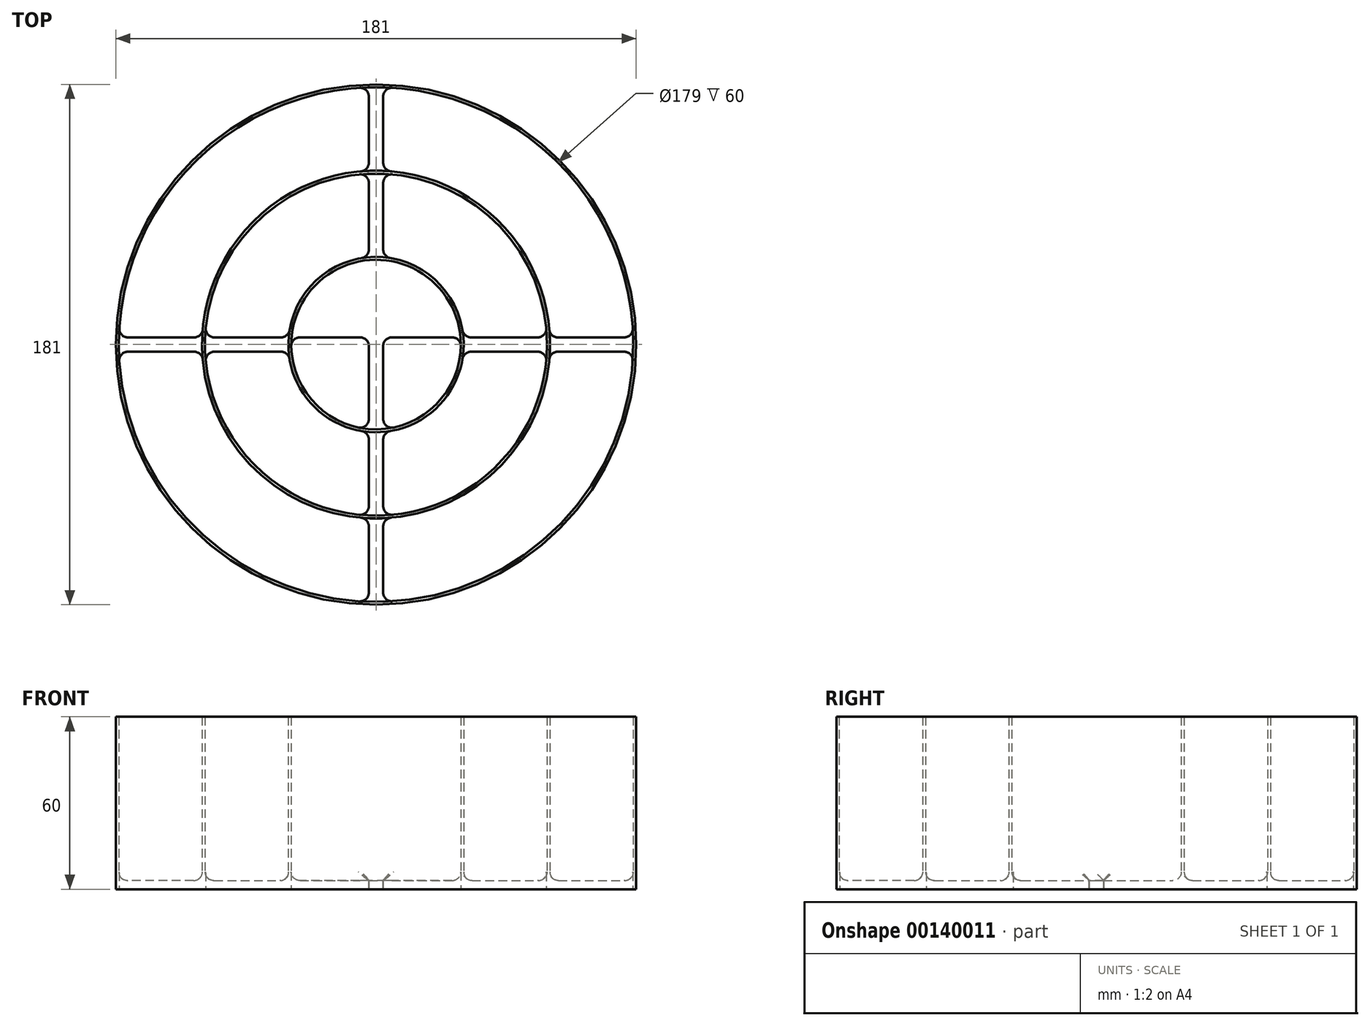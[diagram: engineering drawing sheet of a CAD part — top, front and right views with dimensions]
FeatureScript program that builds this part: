
annotation { "Feature Type Name" : "Feature", "Feature Type Description" : "" }
export const myFeature = defineFeature(function(context is Context, id is Id, definition is map)
    precondition{}
    {
        {
            var Q0;
            Q0=qCreatedBy(makeId("Top.planeOp"),FACE);
            var sketch = newSketch(context, id + "F2", { "sketchPlane" : qUnion([Q0])});
            skCircle(sketch, "E0", {"center": v(0, 0) * mm, "radius": 90.5 * mm});
            skCircle(sketch, "E1", {"center": v(0, 0) * mm, "radius": 89.5 * mm});
            skCircle(sketch, "E2", {"center": v(0, 0) * mm, "radius": 60.5 * mm});
            skCircle(sketch, "E3", {"center": v(0, 0) * mm, "radius": 59.5 * mm});
            skCircle(sketch, "E4", {"center": v(0, 0) * mm, "radius": 30.5 * mm});
            skCircle(sketch, "E5", {"center": v(0, 0) * mm, "radius": 29.5 * mm});
            skLineSegment(sketch, "E6", {"start": v(-59.45, 2.5) * mm, "end": v(-30.4, 2.5) * mm});
            skLineSegment(sketch, "E7", {"start": v(-59.45, -2.5) * mm, "end": v(-30.4, -2.5) * mm});
            skLineSegment(sketch, "E8", {"start": v(-60.45, 2.5) * mm, "end": v(-89.47, 2.5) * mm});
            skLineSegment(sketch, "E9", {"start": v(-60.45, -2.5) * mm, "end": v(-89.47, -2.5) * mm});
            skLineSegment(sketch, "E10", {"start": v(-29.4, 2.5) * mm, "end": v(29.4, 2.5) * mm});
            skLineSegment(sketch, "E11", {"start": v(-29.4, -2.5) * mm, "end": v(29.4, -2.5) * mm});
            skLineSegment(sketch, "E12", {"start": v(30.4, 2.5) * mm, "end": v(59.45, 2.5) * mm});
            skLineSegment(sketch, "E13", {"start": v(60.45, 2.5) * mm, "end": v(89.47, 2.5) * mm});
            skLineSegment(sketch, "E14", {"start": v(30.4, -2.5) * mm, "end": v(59.45, -2.5) * mm});
            skLineSegment(sketch, "E15", {"start": v(60.45, -2.5) * mm, "end": v(89.47, -2.5) * mm});
            skLineSegment(sketch, "E16", {"start": v(2.5, -60.45) * mm, "end": v(2.5, -89.47) * mm});
            skLineSegment(sketch, "E17", {"start": v(-2.5, -60.45) * mm, "end": v(-2.5, -89.47) * mm});
            skLineSegment(sketch, "E18", {"start": v(2.5, -59.45) * mm, "end": v(2.5, -30.4) * mm});
            skLineSegment(sketch, "E19", {"start": v(-2.5, -59.45) * mm, "end": v(-2.5, -30.4) * mm});
            skLineSegment(sketch, "E20", {"start": v(2.5, -29.4) * mm, "end": v(2.5, 29.4) * mm});
            skLineSegment(sketch, "E21", {"start": v(-2.5, -29.4) * mm, "end": v(-2.5, 29.4) * mm});
            skLineSegment(sketch, "E22", {"start": v(2.5, 30.4) * mm, "end": v(2.5, 59.45) * mm});
            skLineSegment(sketch, "E23", {"start": v(-2.5, 30.4) * mm, "end": v(-2.5, 59.45) * mm});
            skLineSegment(sketch, "E24", {"start": v(2.5, 60.45) * mm, "end": v(2.5, 89.47) * mm});
            skLineSegment(sketch, "E25", {"start": v(-2.5, 60.45) * mm, "end": v(-2.5, 89.47) * mm});
            skSolve(sketch);
        }
        {
            var Q0;
            {var subQ0=sQuery(id+"F2.wireOp",EDGE,"E24");Q0=makeQuery(id+"F2.imprint","IMPRINT",FACE,{"disambiguationData":[TD([[makeQuery(id+"F2.imprint","IMPRINT",EDGE,{"derivedFrom":subQ0}),1.0]])]});}
            var Q1;
            {var subQ0=sQuery(id+"F2.wireOp",EDGE,"E22");Q1=makeQuery(id+"F2.imprint","IMPRINT",FACE,{"disambiguationData":[TD([[makeQuery(id+"F2.imprint","IMPRINT",EDGE,{"derivedFrom":subQ0}),1.0]])]});}
            var Q2;
            {var subQ0=sQuery(id+"F2.wireOp",EDGE,"E20");var subQ1=sQuery(id+"F2.wireOp",EDGE,"E5");var subQ2=makeQuery(id+"F2.imprint","INTERSECT",VERTEX,{"disambiguationData":[OD(1.0)],"derivedFrom":[subQ1,subQ0]});Q2=makeQuery(id+"F2.imprint","IMPRINT",FACE,{"disambiguationData":[TD([[makeQuery(id+"F2.imprint","IMPRINT",EDGE,{"disambiguationData":[TD([[subQ2,-1.0]])],"derivedFrom":subQ1}),1.0]])]});}
            var Q3;
            {var subQ0=sQuery(id+"F2.wireOp",EDGE,"E10");var subQ1=sQuery(id+"F2.wireOp",EDGE,"E5");var subQ2=makeQuery(id+"F2.imprint","INTERSECT",VERTEX,{"disambiguationData":[OD(0.0)],"derivedFrom":[subQ1,subQ0]});Q3=makeQuery(id+"F2.imprint","IMPRINT",FACE,{"disambiguationData":[TD([[makeQuery(id+"F2.imprint","IMPRINT",EDGE,{"disambiguationData":[TD([[subQ2,-1.0]])],"derivedFrom":subQ1}),1.0]])]});}
            var Q4;
            {var subQ0=sQuery(id+"F2.wireOp",EDGE,"E10");var subQ1=sQuery(id+"F2.wireOp",EDGE,"E5");var subQ2=makeQuery(id+"F2.imprint","INTERSECT",VERTEX,{"disambiguationData":[OD(1.0)],"derivedFrom":[subQ1,subQ0]});Q4=makeQuery(id+"F2.imprint","IMPRINT",FACE,{"disambiguationData":[TD([[makeQuery(id+"F2.imprint","IMPRINT",EDGE,{"disambiguationData":[TD([[subQ2,1.0]])],"derivedFrom":subQ1}),1.0]])]});}
            var Q5;
            {var subQ0=sQuery(id+"F2.wireOp",EDGE,"E20");var subQ1=sQuery(id+"F2.wireOp",EDGE,"E5");var subQ2=makeQuery(id+"F2.imprint","INTERSECT",VERTEX,{"disambiguationData":[OD(0.0)],"derivedFrom":[subQ1,subQ0]});Q5=makeQuery(id+"F2.imprint","IMPRINT",FACE,{"disambiguationData":[TD([[makeQuery(id+"F2.imprint","IMPRINT",EDGE,{"disambiguationData":[TD([[subQ2,1.0]])],"derivedFrom":subQ1}),1.0]])]});}
            var Q6;
            {var subQ0=sQuery(id+"F2.wireOp",EDGE,"E21");var subQ1=sQuery(id+"F2.wireOp",EDGE,"E10");var subQ2=makeQuery(id+"F2.imprint","INTERSECT",VERTEX,{"derivedFrom":[subQ1,subQ0]});Q6=makeQuery(id+"F2.imprint","IMPRINT",FACE,{"disambiguationData":[TD([[makeQuery(id+"F2.imprint","IMPRINT",EDGE,{"disambiguationData":[TD([[subQ2,-1.0]])],"derivedFrom":subQ1}),-1.0]])]});}
            var Q7;
            {var subQ0=sQuery(id+"F2.wireOp",EDGE,"E18");Q7=makeQuery(id+"F2.imprint","IMPRINT",FACE,{"disambiguationData":[TD([[makeQuery(id+"F2.imprint","IMPRINT",EDGE,{"derivedFrom":subQ0}),1.0]])]});}
            var Q8;
            {var subQ0=sQuery(id+"F2.wireOp",EDGE,"E16");Q8=makeQuery(id+"F2.imprint","IMPRINT",FACE,{"disambiguationData":[TD([[makeQuery(id+"F2.imprint","IMPRINT",EDGE,{"derivedFrom":subQ0}),-1.0]])]});}
            var Q9;
            {var subQ0=sQuery(id+"F2.wireOp",EDGE,"E6");Q9=makeQuery(id+"F2.imprint","IMPRINT",FACE,{"disambiguationData":[TD([[makeQuery(id+"F2.imprint","IMPRINT",EDGE,{"derivedFrom":subQ0}),-1.0]])]});}
            var Q10;
            {var subQ0=sQuery(id+"F2.wireOp",EDGE,"E8");Q10=makeQuery(id+"F2.imprint","IMPRINT",FACE,{"disambiguationData":[TD([[makeQuery(id+"F2.imprint","IMPRINT",EDGE,{"derivedFrom":subQ0}),1.0]])]});}
            var Q11;
            {var subQ0=sQuery(id+"F2.wireOp",EDGE,"E13");Q11=makeQuery(id+"F2.imprint","IMPRINT",FACE,{"disambiguationData":[TD([[makeQuery(id+"F2.imprint","IMPRINT",EDGE,{"derivedFrom":subQ0}),-1.0]])]});}
            var Q12;
            {var subQ0=sQuery(id+"F2.wireOp",EDGE,"E12");Q12=makeQuery(id+"F2.imprint","IMPRINT",FACE,{"disambiguationData":[TD([[makeQuery(id+"F2.imprint","IMPRINT",EDGE,{"derivedFrom":subQ0}),-1.0]])]});}
            var Q13;
            {var subQ0=sQuery(id+"F2.wireOp",EDGE,"E2");var subQ16=makeQuery(id+"F2.imprint","INTERSECT",VERTEX,{"derivedFrom":[subQ0,sQuery(id+"F2.wireOp",EDGE,"E13")]});Q13=makeQuery(id+"F2.imprint","IMPRINT",FACE,{"disambiguationData":[TD([[makeQuery(id+"F2.imprint","IMPRINT",EDGE,{"disambiguationData":[TD([[subQ16,-1.0]])],"derivedFrom":subQ0}),1.0]])]});}
            var Q14;
            {var subQ5=sQuery(id+"F2.wireOp",EDGE,"E4");var subQ19=makeQuery(id+"F2.imprint","INTERSECT",VERTEX,{"derivedFrom":[subQ5,sQuery(id+"F2.wireOp",EDGE,"E12")]});Q14=makeQuery(id+"F2.imprint","IMPRINT",FACE,{"disambiguationData":[TD([[makeQuery(id+"F2.imprint","IMPRINT",EDGE,{"disambiguationData":[TD([[subQ19,-1.0]])],"derivedFrom":subQ5}),1.0]])]});}
            var Q15;
            Q15=makeQuery(id+"F2.imprint","IMPRINT",FACE,{"disambiguationData":[TD([[makeQuery(id+"F2.imprint","IMPRINT",EDGE,{"derivedFrom":sQuery(id+"F2.wireOp",EDGE,"E0")}),1.0]])]});
            extrude(context, id + "F3", {"entities" : qUnion([Q0, Q1, Q2, Q3, Q4, Q5, Q6, Q7, Q8, Q9, Q10, Q11, Q12, Q13, Q14, Q15]), "depth" : 3 * mm});
        }
        {
            var Q0;
            Q0=makeQuery(id+"F2.imprint","IMPRINT",FACE,{"disambiguationData":[TD([[makeQuery(id+"F2.imprint","IMPRINT",EDGE,{"derivedFrom":sQuery(id+"F2.wireOp",EDGE,"E0")}),1.0]])]});
            var Q1;
            {var subQ0=sQuery(id+"F2.wireOp",EDGE,"E2");var subQ16=makeQuery(id+"F2.imprint","INTERSECT",VERTEX,{"derivedFrom":[subQ0,sQuery(id+"F2.wireOp",EDGE,"E13")]});Q1=makeQuery(id+"F2.imprint","IMPRINT",FACE,{"disambiguationData":[TD([[makeQuery(id+"F2.imprint","IMPRINT",EDGE,{"disambiguationData":[TD([[subQ16,-1.0]])],"derivedFrom":subQ0}),1.0]])]});}
            var Q2;
            {var subQ5=sQuery(id+"F2.wireOp",EDGE,"E4");var subQ19=makeQuery(id+"F2.imprint","INTERSECT",VERTEX,{"derivedFrom":[subQ5,sQuery(id+"F2.wireOp",EDGE,"E12")]});Q2=makeQuery(id+"F2.imprint","IMPRINT",FACE,{"disambiguationData":[TD([[makeQuery(id+"F2.imprint","IMPRINT",EDGE,{"disambiguationData":[TD([[subQ19,-1.0]])],"derivedFrom":subQ5}),1.0]])]});}
            extrude(context, id + "F0", {"entities" : qUnion([Q0, Q1, Q2]), "operationType" : NewBodyOperationType.ADD, "depth" : 60 * mm});
        }
        {
            var Q0;
            Q0=makeQuery(id+"F3.opExtrude","SWEPT_EDGE",EDGE,{"disambiguationData":[OSD([sQuery(id+"F2.wireOp",EDGE,"E2"),sQuery(id+"F2.wireOp",EDGE,"E24")])]});
            var Q1;
            Q1=makeQuery(id+"F3.opExtrude","SWEPT_EDGE",EDGE,{"disambiguationData":[OSD([sQuery(id+"F2.wireOp",EDGE,"E4"),sQuery(id+"F2.wireOp",EDGE,"E22")])]});
            var Q2;
            Q2=makeQuery(id+"F3.opExtrude","SWEPT_EDGE",EDGE,{"disambiguationData":[OSD([sQuery(id+"F2.wireOp",EDGE,"E10"),sQuery(id+"F2.wireOp",EDGE,"E20")])]});
            var Q3;
            Q3=makeQuery(id+"F3.opExtrude","SWEPT_EDGE",EDGE,{"disambiguationData":[OSD([sQuery(id+"F2.wireOp",EDGE,"E4"),sQuery(id+"F2.wireOp",EDGE,"E12")])]});
            var Q4;
            Q4=makeQuery(id+"F3.opExtrude","SWEPT_EDGE",EDGE,{"disambiguationData":[OSD([sQuery(id+"F2.wireOp",EDGE,"E2"),sQuery(id+"F2.wireOp",EDGE,"E13")])]});
            var Q5;
            Q5=makeQuery(id+"F3.opExtrude","SWEPT_EDGE",EDGE,{"disambiguationData":[OSD([sQuery(id+"F2.wireOp",EDGE,"E1"),sQuery(id+"F2.wireOp",EDGE,"E16")])]});
            var Q6;
            Q6=makeQuery(id+"F3.opExtrude","SWEPT_EDGE",EDGE,{"disambiguationData":[OSD([sQuery(id+"F2.wireOp",EDGE,"E3"),sQuery(id+"F2.wireOp",EDGE,"E18")])]});
            var Q7;
            {var subQ0=sQuery(id+"F2.wireOp",EDGE,"E20");var subQ1=sQuery(id+"F2.wireOp",EDGE,"E5");Q7=makeQuery(id+"F3.opExtrude","SWEPT_EDGE",EDGE,{"disambiguationData":[OSD([subQ1,subQ0]),TDD([makeQuery(id+"F2.imprint","INTERSECT",VERTEX,{"disambiguationData":[OD(0.0)],"derivedFrom":[subQ1,subQ0]})])]});}
            var Q8;
            {var subQ0=sQuery(id+"F2.wireOp",EDGE,"E10");var subQ1=sQuery(id+"F2.wireOp",EDGE,"E5");Q8=makeQuery(id+"F3.opExtrude","SWEPT_EDGE",EDGE,{"disambiguationData":[OSD([subQ1,subQ0]),TDD([makeQuery(id+"F2.imprint","INTERSECT",VERTEX,{"disambiguationData":[OD(0.0)],"derivedFrom":[subQ1,subQ0]})])]});}
            var Q9;
            Q9=makeQuery(id+"F3.opExtrude","SWEPT_EDGE",EDGE,{"disambiguationData":[OSD([sQuery(id+"F2.wireOp",EDGE,"E3"),sQuery(id+"F2.wireOp",EDGE,"E6")])]});
            var Q10;
            Q10=makeQuery(id+"F3.opExtrude","SWEPT_EDGE",EDGE,{"disambiguationData":[OSD([sQuery(id+"F2.wireOp",EDGE,"E1"),sQuery(id+"F2.wireOp",EDGE,"E8")])]});
            var Q11;
            Q11=makeQuery(id+"F3.opExtrude","SWEPT_EDGE",EDGE,{"disambiguationData":[OSD([sQuery(id+"F2.wireOp",EDGE,"E2"),sQuery(id+"F2.wireOp",EDGE,"E25")])]});
            var Q12;
            Q12=makeQuery(id+"F3.opExtrude","SWEPT_EDGE",EDGE,{"disambiguationData":[OSD([sQuery(id+"F2.wireOp",EDGE,"E4"),sQuery(id+"F2.wireOp",EDGE,"E23")])]});
            var Q13;
            Q13=makeQuery(id+"F3.opExtrude","SWEPT_EDGE",EDGE,{"disambiguationData":[OSD([sQuery(id+"F2.wireOp",EDGE,"E10"),sQuery(id+"F2.wireOp",EDGE,"E21")])]});
            var Q14;
            Q14=makeQuery(id+"F3.opExtrude","SWEPT_EDGE",EDGE,{"disambiguationData":[OSD([sQuery(id+"F2.wireOp",EDGE,"E4"),sQuery(id+"F2.wireOp",EDGE,"E6")])]});
            var Q15;
            Q15=makeQuery(id+"F3.opExtrude","SWEPT_EDGE",EDGE,{"disambiguationData":[OSD([sQuery(id+"F2.wireOp",EDGE,"E2"),sQuery(id+"F2.wireOp",EDGE,"E8")])]});
            var Q16;
            {var subQ0=sQuery(id+"F2.wireOp",EDGE,"E21");var subQ1=sQuery(id+"F2.wireOp",EDGE,"E5");Q16=makeQuery(id+"F3.opExtrude","SWEPT_EDGE",EDGE,{"disambiguationData":[OSD([subQ1,subQ0]),TDD([makeQuery(id+"F2.imprint","INTERSECT",VERTEX,{"disambiguationData":[OD(0.0)],"derivedFrom":[subQ1,subQ0]})])]});}
            var Q17;
            Q17=makeQuery(id+"F3.opExtrude","SWEPT_EDGE",EDGE,{"disambiguationData":[OSD([sQuery(id+"F2.wireOp",EDGE,"E3"),sQuery(id+"F2.wireOp",EDGE,"E19")])]});
            var Q18;
            Q18=makeQuery(id+"F3.opExtrude","SWEPT_EDGE",EDGE,{"disambiguationData":[OSD([sQuery(id+"F2.wireOp",EDGE,"E1"),sQuery(id+"F2.wireOp",EDGE,"E17")])]});
            var Q19;
            {var subQ0=sQuery(id+"F2.wireOp",EDGE,"E10");var subQ1=sQuery(id+"F2.wireOp",EDGE,"E5");Q19=makeQuery(id+"F3.opExtrude","SWEPT_EDGE",EDGE,{"disambiguationData":[OSD([subQ1,subQ0]),TDD([makeQuery(id+"F2.imprint","INTERSECT",VERTEX,{"disambiguationData":[OD(1.0)],"derivedFrom":[subQ1,subQ0]})])]});}
            var Q20;
            Q20=makeQuery(id+"F3.opExtrude","SWEPT_EDGE",EDGE,{"disambiguationData":[OSD([sQuery(id+"F2.wireOp",EDGE,"E3"),sQuery(id+"F2.wireOp",EDGE,"E12")])]});
            var Q21;
            Q21=makeQuery(id+"F3.opExtrude","SWEPT_EDGE",EDGE,{"disambiguationData":[OSD([sQuery(id+"F2.wireOp",EDGE,"E1"),sQuery(id+"F2.wireOp",EDGE,"E13")])]});
            var Q22;
            Q22=makeQuery(id+"F3.opExtrude","SWEPT_EDGE",EDGE,{"disambiguationData":[OSD([sQuery(id+"F2.wireOp",EDGE,"E2"),sQuery(id+"F2.wireOp",EDGE,"E9")])]});
            var Q23;
            Q23=makeQuery(id+"F3.opExtrude","SWEPT_EDGE",EDGE,{"disambiguationData":[OSD([sQuery(id+"F2.wireOp",EDGE,"E4"),sQuery(id+"F2.wireOp",EDGE,"E7")])]});
            var Q24;
            Q24=makeQuery(id+"F3.opExtrude","SWEPT_EDGE",EDGE,{"disambiguationData":[OSD([sQuery(id+"F2.wireOp",EDGE,"E11"),sQuery(id+"F2.wireOp",EDGE,"E21")])]});
            var Q25;
            Q25=makeQuery(id+"F3.opExtrude","SWEPT_EDGE",EDGE,{"disambiguationData":[OSD([sQuery(id+"F2.wireOp",EDGE,"E4"),sQuery(id+"F2.wireOp",EDGE,"E19")])]});
            var Q26;
            Q26=makeQuery(id+"F3.opExtrude","SWEPT_EDGE",EDGE,{"disambiguationData":[OSD([sQuery(id+"F2.wireOp",EDGE,"E2"),sQuery(id+"F2.wireOp",EDGE,"E17")])]});
            var Q27;
            {var subQ0=sQuery(id+"F2.wireOp",EDGE,"E11");var subQ1=sQuery(id+"F2.wireOp",EDGE,"E5");Q27=makeQuery(id+"F3.opExtrude","SWEPT_EDGE",EDGE,{"disambiguationData":[OSD([subQ1,subQ0]),TDD([makeQuery(id+"F2.imprint","INTERSECT",VERTEX,{"disambiguationData":[OD(1.0)],"derivedFrom":[subQ1,subQ0]})])]});}
            var Q28;
            Q28=makeQuery(id+"F3.opExtrude","SWEPT_EDGE",EDGE,{"disambiguationData":[OSD([sQuery(id+"F2.wireOp",EDGE,"E3"),sQuery(id+"F2.wireOp",EDGE,"E14")])]});
            var Q29;
            Q29=makeQuery(id+"F3.opExtrude","SWEPT_EDGE",EDGE,{"disambiguationData":[OSD([sQuery(id+"F2.wireOp",EDGE,"E1"),sQuery(id+"F2.wireOp",EDGE,"E15")])]});
            var Q30;
            {var subQ0=sQuery(id+"F2.wireOp",EDGE,"E21");var subQ1=sQuery(id+"F2.wireOp",EDGE,"E5");Q30=makeQuery(id+"F3.opExtrude","SWEPT_EDGE",EDGE,{"disambiguationData":[OSD([subQ1,subQ0]),TDD([makeQuery(id+"F2.imprint","INTERSECT",VERTEX,{"disambiguationData":[OD(1.0)],"derivedFrom":[subQ1,subQ0]})])]});}
            var Q31;
            Q31=makeQuery(id+"F3.opExtrude","SWEPT_EDGE",EDGE,{"disambiguationData":[OSD([sQuery(id+"F2.wireOp",EDGE,"E3"),sQuery(id+"F2.wireOp",EDGE,"E23")])]});
            var Q32;
            Q32=makeQuery(id+"F3.opExtrude","SWEPT_EDGE",EDGE,{"disambiguationData":[OSD([sQuery(id+"F2.wireOp",EDGE,"E1"),sQuery(id+"F2.wireOp",EDGE,"E25")])]});
            var Q33;
            Q33=makeQuery(id+"F3.opExtrude","SWEPT_EDGE",EDGE,{"disambiguationData":[OSD([sQuery(id+"F2.wireOp",EDGE,"E2"),sQuery(id+"F2.wireOp",EDGE,"E16")])]});
            var Q34;
            Q34=makeQuery(id+"F3.opExtrude","SWEPT_EDGE",EDGE,{"disambiguationData":[OSD([sQuery(id+"F2.wireOp",EDGE,"E4"),sQuery(id+"F2.wireOp",EDGE,"E18")])]});
            var Q35;
            {var subQ0=sQuery(id+"F2.wireOp",EDGE,"E11");var subQ1=sQuery(id+"F2.wireOp",EDGE,"E5");Q35=makeQuery(id+"F3.opExtrude","SWEPT_EDGE",EDGE,{"disambiguationData":[OSD([subQ1,subQ0]),TDD([makeQuery(id+"F2.imprint","INTERSECT",VERTEX,{"disambiguationData":[OD(0.0)],"derivedFrom":[subQ1,subQ0]})])]});}
            var Q36;
            Q36=makeQuery(id+"F3.opExtrude","SWEPT_EDGE",EDGE,{"disambiguationData":[OSD([sQuery(id+"F2.wireOp",EDGE,"E3"),sQuery(id+"F2.wireOp",EDGE,"E7")])]});
            var Q37;
            Q37=makeQuery(id+"F3.opExtrude","SWEPT_EDGE",EDGE,{"disambiguationData":[OSD([sQuery(id+"F2.wireOp",EDGE,"E1"),sQuery(id+"F2.wireOp",EDGE,"E9")])]});
            var Q38;
            Q38=makeQuery(id+"F3.opExtrude","SWEPT_EDGE",EDGE,{"disambiguationData":[OSD([sQuery(id+"F2.wireOp",EDGE,"E11"),sQuery(id+"F2.wireOp",EDGE,"E20")])]});
            var Q39;
            Q39=makeQuery(id+"F3.opExtrude","SWEPT_EDGE",EDGE,{"disambiguationData":[OSD([sQuery(id+"F2.wireOp",EDGE,"E4"),sQuery(id+"F2.wireOp",EDGE,"E14")])]});
            var Q40;
            {var subQ0=sQuery(id+"F2.wireOp",EDGE,"E20");var subQ1=sQuery(id+"F2.wireOp",EDGE,"E5");Q40=makeQuery(id+"F3.opExtrude","SWEPT_EDGE",EDGE,{"disambiguationData":[OSD([subQ1,subQ0]),TDD([makeQuery(id+"F2.imprint","INTERSECT",VERTEX,{"disambiguationData":[OD(1.0)],"derivedFrom":[subQ1,subQ0]})])]});}
            var Q41;
            Q41=makeQuery(id+"F3.opExtrude","SWEPT_EDGE",EDGE,{"disambiguationData":[OSD([sQuery(id+"F2.wireOp",EDGE,"E2"),sQuery(id+"F2.wireOp",EDGE,"E15")])]});
            var Q42;
            Q42=makeQuery(id+"F3.opExtrude","SWEPT_EDGE",EDGE,{"disambiguationData":[OSD([sQuery(id+"F2.wireOp",EDGE,"E3"),sQuery(id+"F2.wireOp",EDGE,"E22")])]});
            var Q43;
            Q43=makeQuery(id+"F3.opExtrude","SWEPT_EDGE",EDGE,{"disambiguationData":[OSD([sQuery(id+"F2.wireOp",EDGE,"E1"),sQuery(id+"F2.wireOp",EDGE,"E24")])]});
            fillet(context, id + "F1", {"entities" : qUnion([Q0, Q1, Q2, Q3, Q4, Q5, Q6, Q7, Q8, Q9, Q10, Q11, Q12, Q13, Q14, Q15, Q16, Q17, Q18, Q19, Q20, Q21, Q22, Q23, Q24, Q25, Q26, Q27, Q28, Q29, Q30, Q31, Q32, Q33, Q34, Q35, Q36, Q37, Q38, Q39, Q40, Q41, Q42, Q43]), "radius" : 3 * mm, "tangentPropagation" : true, "allowEdgeOverflow" : false});
        }
        {
            var Q0;
            {var subQ0=sQuery(id+"F2.wireOp",EDGE,"E1");Q0=makeQuery(id+"F0.boolean.opBoolean","INTERSECT",EDGE,{"disambiguationData":[OD(1.0)],"derivedFrom":[makeQuery(id+"F3.opExtrude","CAP_FACE",FACE,{"disambiguationData":[OSD([sQuery(id+"F2.wireOp",EDGE,"E0"),subQ0,sQuery(id+"F2.wireOp",EDGE,"E2"),sQuery(id+"F2.wireOp",EDGE,"E3"),sQuery(id+"F2.wireOp",EDGE,"E4"),sQuery(id+"F2.wireOp",EDGE,"E5"),sQuery(id+"F2.wireOp",EDGE,"E6"),sQuery(id+"F2.wireOp",EDGE,"E7"),sQuery(id+"F2.wireOp",EDGE,"E8"),sQuery(id+"F2.wireOp",EDGE,"E9"),sQuery(id+"F2.wireOp",EDGE,"E10"),sQuery(id+"F2.wireOp",EDGE,"E11"),sQuery(id+"F2.wireOp",EDGE,"E12"),sQuery(id+"F2.wireOp",EDGE,"E13"),sQuery(id+"F2.wireOp",EDGE,"E14"),sQuery(id+"F2.wireOp",EDGE,"E15"),sQuery(id+"F2.wireOp",EDGE,"E16"),sQuery(id+"F2.wireOp",EDGE,"E17"),sQuery(id+"F2.wireOp",EDGE,"E18"),sQuery(id+"F2.wireOp",EDGE,"E19"),sQuery(id+"F2.wireOp",EDGE,"E20"),sQuery(id+"F2.wireOp",EDGE,"E21"),sQuery(id+"F2.wireOp",EDGE,"E22"),sQuery(id+"F2.wireOp",EDGE,"E23"),sQuery(id+"F2.wireOp",EDGE,"E24"),sQuery(id+"F2.wireOp",EDGE,"E25")])],"isStart":false}),makeQuery(id+"F0.opExtrude","SWEPT_FACE",FACE,{"disambiguationData":[OSD([subQ0])]})]});}
            var Q1;
            {var subQ0=sQuery(id+"F2.wireOp",EDGE,"E3");Q1=makeQuery(id+"F0.boolean.opBoolean","INTERSECT",EDGE,{"disambiguationData":[OD(1.0)],"derivedFrom":[makeQuery(id+"F3.opExtrude","CAP_FACE",FACE,{"disambiguationData":[OSD([sQuery(id+"F2.wireOp",EDGE,"E0"),sQuery(id+"F2.wireOp",EDGE,"E1"),sQuery(id+"F2.wireOp",EDGE,"E2"),subQ0,sQuery(id+"F2.wireOp",EDGE,"E4"),sQuery(id+"F2.wireOp",EDGE,"E5"),sQuery(id+"F2.wireOp",EDGE,"E6"),sQuery(id+"F2.wireOp",EDGE,"E7"),sQuery(id+"F2.wireOp",EDGE,"E8"),sQuery(id+"F2.wireOp",EDGE,"E9"),sQuery(id+"F2.wireOp",EDGE,"E10"),sQuery(id+"F2.wireOp",EDGE,"E11"),sQuery(id+"F2.wireOp",EDGE,"E12"),sQuery(id+"F2.wireOp",EDGE,"E13"),sQuery(id+"F2.wireOp",EDGE,"E14"),sQuery(id+"F2.wireOp",EDGE,"E15"),sQuery(id+"F2.wireOp",EDGE,"E16"),sQuery(id+"F2.wireOp",EDGE,"E17"),sQuery(id+"F2.wireOp",EDGE,"E18"),sQuery(id+"F2.wireOp",EDGE,"E19"),sQuery(id+"F2.wireOp",EDGE,"E20"),sQuery(id+"F2.wireOp",EDGE,"E21"),sQuery(id+"F2.wireOp",EDGE,"E22"),sQuery(id+"F2.wireOp",EDGE,"E23"),sQuery(id+"F2.wireOp",EDGE,"E24"),sQuery(id+"F2.wireOp",EDGE,"E25")])],"isStart":false}),makeQuery(id+"F0.opExtrude","SWEPT_FACE",FACE,{"disambiguationData":[OSD([subQ0])]})]});}
            var Q2;
            {var subQ0=sQuery(id+"F2.wireOp",EDGE,"E5");Q2=makeQuery(id+"F0.boolean.opBoolean","INTERSECT",EDGE,{"disambiguationData":[OD(1.0)],"derivedFrom":[makeQuery(id+"F3.opExtrude","CAP_FACE",FACE,{"disambiguationData":[OSD([sQuery(id+"F2.wireOp",EDGE,"E0"),sQuery(id+"F2.wireOp",EDGE,"E1"),sQuery(id+"F2.wireOp",EDGE,"E2"),sQuery(id+"F2.wireOp",EDGE,"E3"),sQuery(id+"F2.wireOp",EDGE,"E4"),subQ0,sQuery(id+"F2.wireOp",EDGE,"E6"),sQuery(id+"F2.wireOp",EDGE,"E7"),sQuery(id+"F2.wireOp",EDGE,"E8"),sQuery(id+"F2.wireOp",EDGE,"E9"),sQuery(id+"F2.wireOp",EDGE,"E10"),sQuery(id+"F2.wireOp",EDGE,"E11"),sQuery(id+"F2.wireOp",EDGE,"E12"),sQuery(id+"F2.wireOp",EDGE,"E13"),sQuery(id+"F2.wireOp",EDGE,"E14"),sQuery(id+"F2.wireOp",EDGE,"E15"),sQuery(id+"F2.wireOp",EDGE,"E16"),sQuery(id+"F2.wireOp",EDGE,"E17"),sQuery(id+"F2.wireOp",EDGE,"E18"),sQuery(id+"F2.wireOp",EDGE,"E19"),sQuery(id+"F2.wireOp",EDGE,"E20"),sQuery(id+"F2.wireOp",EDGE,"E21"),sQuery(id+"F2.wireOp",EDGE,"E22"),sQuery(id+"F2.wireOp",EDGE,"E23"),sQuery(id+"F2.wireOp",EDGE,"E24"),sQuery(id+"F2.wireOp",EDGE,"E25")])],"isStart":false}),makeQuery(id+"F0.opExtrude","SWEPT_FACE",FACE,{"disambiguationData":[OSD([subQ0])]})]});}
            var Q3;
            {var subQ0=sQuery(id+"F2.wireOp",EDGE,"E4");Q3=makeQuery(id+"F0.boolean.opBoolean","INTERSECT",EDGE,{"disambiguationData":[OD(0.0)],"derivedFrom":[makeQuery(id+"F3.opExtrude","CAP_FACE",FACE,{"disambiguationData":[OSD([sQuery(id+"F2.wireOp",EDGE,"E0"),sQuery(id+"F2.wireOp",EDGE,"E1"),sQuery(id+"F2.wireOp",EDGE,"E2"),sQuery(id+"F2.wireOp",EDGE,"E3"),subQ0,sQuery(id+"F2.wireOp",EDGE,"E5"),sQuery(id+"F2.wireOp",EDGE,"E6"),sQuery(id+"F2.wireOp",EDGE,"E7"),sQuery(id+"F2.wireOp",EDGE,"E8"),sQuery(id+"F2.wireOp",EDGE,"E9"),sQuery(id+"F2.wireOp",EDGE,"E10"),sQuery(id+"F2.wireOp",EDGE,"E11"),sQuery(id+"F2.wireOp",EDGE,"E12"),sQuery(id+"F2.wireOp",EDGE,"E13"),sQuery(id+"F2.wireOp",EDGE,"E14"),sQuery(id+"F2.wireOp",EDGE,"E15"),sQuery(id+"F2.wireOp",EDGE,"E16"),sQuery(id+"F2.wireOp",EDGE,"E17"),sQuery(id+"F2.wireOp",EDGE,"E18"),sQuery(id+"F2.wireOp",EDGE,"E19"),sQuery(id+"F2.wireOp",EDGE,"E20"),sQuery(id+"F2.wireOp",EDGE,"E21"),sQuery(id+"F2.wireOp",EDGE,"E22"),sQuery(id+"F2.wireOp",EDGE,"E23"),sQuery(id+"F2.wireOp",EDGE,"E24"),sQuery(id+"F2.wireOp",EDGE,"E25")])],"isStart":false}),makeQuery(id+"F0.opExtrude","SWEPT_FACE",FACE,{"disambiguationData":[OSD([subQ0])]})]});}
            var Q4;
            {var subQ0=sQuery(id+"F2.wireOp",EDGE,"E2");Q4=makeQuery(id+"F0.boolean.opBoolean","INTERSECT",EDGE,{"disambiguationData":[OD(0.0)],"derivedFrom":[makeQuery(id+"F3.opExtrude","CAP_FACE",FACE,{"disambiguationData":[OSD([sQuery(id+"F2.wireOp",EDGE,"E0"),sQuery(id+"F2.wireOp",EDGE,"E1"),subQ0,sQuery(id+"F2.wireOp",EDGE,"E3"),sQuery(id+"F2.wireOp",EDGE,"E4"),sQuery(id+"F2.wireOp",EDGE,"E5"),sQuery(id+"F2.wireOp",EDGE,"E6"),sQuery(id+"F2.wireOp",EDGE,"E7"),sQuery(id+"F2.wireOp",EDGE,"E8"),sQuery(id+"F2.wireOp",EDGE,"E9"),sQuery(id+"F2.wireOp",EDGE,"E10"),sQuery(id+"F2.wireOp",EDGE,"E11"),sQuery(id+"F2.wireOp",EDGE,"E12"),sQuery(id+"F2.wireOp",EDGE,"E13"),sQuery(id+"F2.wireOp",EDGE,"E14"),sQuery(id+"F2.wireOp",EDGE,"E15"),sQuery(id+"F2.wireOp",EDGE,"E16"),sQuery(id+"F2.wireOp",EDGE,"E17"),sQuery(id+"F2.wireOp",EDGE,"E18"),sQuery(id+"F2.wireOp",EDGE,"E19"),sQuery(id+"F2.wireOp",EDGE,"E20"),sQuery(id+"F2.wireOp",EDGE,"E21"),sQuery(id+"F2.wireOp",EDGE,"E22"),sQuery(id+"F2.wireOp",EDGE,"E23"),sQuery(id+"F2.wireOp",EDGE,"E24"),sQuery(id+"F2.wireOp",EDGE,"E25")])],"isStart":false}),makeQuery(id+"F0.opExtrude","SWEPT_FACE",FACE,{"disambiguationData":[OSD([subQ0])]})]});}
            var Q5;
            {var subQ0=sQuery(id+"F2.wireOp",EDGE,"E2");Q5=makeQuery(id+"F0.boolean.opBoolean","INTERSECT",EDGE,{"disambiguationData":[OD(3.0)],"derivedFrom":[makeQuery(id+"F3.opExtrude","CAP_FACE",FACE,{"disambiguationData":[OSD([sQuery(id+"F2.wireOp",EDGE,"E0"),sQuery(id+"F2.wireOp",EDGE,"E1"),subQ0,sQuery(id+"F2.wireOp",EDGE,"E3"),sQuery(id+"F2.wireOp",EDGE,"E4"),sQuery(id+"F2.wireOp",EDGE,"E5"),sQuery(id+"F2.wireOp",EDGE,"E6"),sQuery(id+"F2.wireOp",EDGE,"E7"),sQuery(id+"F2.wireOp",EDGE,"E8"),sQuery(id+"F2.wireOp",EDGE,"E9"),sQuery(id+"F2.wireOp",EDGE,"E10"),sQuery(id+"F2.wireOp",EDGE,"E11"),sQuery(id+"F2.wireOp",EDGE,"E12"),sQuery(id+"F2.wireOp",EDGE,"E13"),sQuery(id+"F2.wireOp",EDGE,"E14"),sQuery(id+"F2.wireOp",EDGE,"E15"),sQuery(id+"F2.wireOp",EDGE,"E16"),sQuery(id+"F2.wireOp",EDGE,"E17"),sQuery(id+"F2.wireOp",EDGE,"E18"),sQuery(id+"F2.wireOp",EDGE,"E19"),sQuery(id+"F2.wireOp",EDGE,"E20"),sQuery(id+"F2.wireOp",EDGE,"E21"),sQuery(id+"F2.wireOp",EDGE,"E22"),sQuery(id+"F2.wireOp",EDGE,"E23"),sQuery(id+"F2.wireOp",EDGE,"E24"),sQuery(id+"F2.wireOp",EDGE,"E25")])],"isStart":false}),makeQuery(id+"F0.opExtrude","SWEPT_FACE",FACE,{"disambiguationData":[OSD([subQ0])]})]});}
            var Q6;
            {var subQ0=sQuery(id+"F2.wireOp",EDGE,"E4");Q6=makeQuery(id+"F0.boolean.opBoolean","INTERSECT",EDGE,{"disambiguationData":[OD(3.0)],"derivedFrom":[makeQuery(id+"F3.opExtrude","CAP_FACE",FACE,{"disambiguationData":[OSD([sQuery(id+"F2.wireOp",EDGE,"E0"),sQuery(id+"F2.wireOp",EDGE,"E1"),sQuery(id+"F2.wireOp",EDGE,"E2"),sQuery(id+"F2.wireOp",EDGE,"E3"),subQ0,sQuery(id+"F2.wireOp",EDGE,"E5"),sQuery(id+"F2.wireOp",EDGE,"E6"),sQuery(id+"F2.wireOp",EDGE,"E7"),sQuery(id+"F2.wireOp",EDGE,"E8"),sQuery(id+"F2.wireOp",EDGE,"E9"),sQuery(id+"F2.wireOp",EDGE,"E10"),sQuery(id+"F2.wireOp",EDGE,"E11"),sQuery(id+"F2.wireOp",EDGE,"E12"),sQuery(id+"F2.wireOp",EDGE,"E13"),sQuery(id+"F2.wireOp",EDGE,"E14"),sQuery(id+"F2.wireOp",EDGE,"E15"),sQuery(id+"F2.wireOp",EDGE,"E16"),sQuery(id+"F2.wireOp",EDGE,"E17"),sQuery(id+"F2.wireOp",EDGE,"E18"),sQuery(id+"F2.wireOp",EDGE,"E19"),sQuery(id+"F2.wireOp",EDGE,"E20"),sQuery(id+"F2.wireOp",EDGE,"E21"),sQuery(id+"F2.wireOp",EDGE,"E22"),sQuery(id+"F2.wireOp",EDGE,"E23"),sQuery(id+"F2.wireOp",EDGE,"E24"),sQuery(id+"F2.wireOp",EDGE,"E25")])],"isStart":false}),makeQuery(id+"F0.opExtrude","SWEPT_FACE",FACE,{"disambiguationData":[OSD([subQ0])]})]});}
            var Q7;
            {var subQ0=sQuery(id+"F2.wireOp",EDGE,"E5");Q7=makeQuery(id+"F0.boolean.opBoolean","INTERSECT",EDGE,{"disambiguationData":[OD(2.0)],"derivedFrom":[makeQuery(id+"F3.opExtrude","CAP_FACE",FACE,{"disambiguationData":[OSD([sQuery(id+"F2.wireOp",EDGE,"E0"),sQuery(id+"F2.wireOp",EDGE,"E1"),sQuery(id+"F2.wireOp",EDGE,"E2"),sQuery(id+"F2.wireOp",EDGE,"E3"),sQuery(id+"F2.wireOp",EDGE,"E4"),subQ0,sQuery(id+"F2.wireOp",EDGE,"E6"),sQuery(id+"F2.wireOp",EDGE,"E7"),sQuery(id+"F2.wireOp",EDGE,"E8"),sQuery(id+"F2.wireOp",EDGE,"E9"),sQuery(id+"F2.wireOp",EDGE,"E10"),sQuery(id+"F2.wireOp",EDGE,"E11"),sQuery(id+"F2.wireOp",EDGE,"E12"),sQuery(id+"F2.wireOp",EDGE,"E13"),sQuery(id+"F2.wireOp",EDGE,"E14"),sQuery(id+"F2.wireOp",EDGE,"E15"),sQuery(id+"F2.wireOp",EDGE,"E16"),sQuery(id+"F2.wireOp",EDGE,"E17"),sQuery(id+"F2.wireOp",EDGE,"E18"),sQuery(id+"F2.wireOp",EDGE,"E19"),sQuery(id+"F2.wireOp",EDGE,"E20"),sQuery(id+"F2.wireOp",EDGE,"E21"),sQuery(id+"F2.wireOp",EDGE,"E22"),sQuery(id+"F2.wireOp",EDGE,"E23"),sQuery(id+"F2.wireOp",EDGE,"E24"),sQuery(id+"F2.wireOp",EDGE,"E25")])],"isStart":false}),makeQuery(id+"F0.opExtrude","SWEPT_FACE",FACE,{"disambiguationData":[OSD([subQ0])]})]});}
            var Q8;
            {var subQ0=sQuery(id+"F2.wireOp",EDGE,"E3");Q8=makeQuery(id+"F0.boolean.opBoolean","INTERSECT",EDGE,{"disambiguationData":[OD(2.0)],"derivedFrom":[makeQuery(id+"F3.opExtrude","CAP_FACE",FACE,{"disambiguationData":[OSD([sQuery(id+"F2.wireOp",EDGE,"E0"),sQuery(id+"F2.wireOp",EDGE,"E1"),sQuery(id+"F2.wireOp",EDGE,"E2"),subQ0,sQuery(id+"F2.wireOp",EDGE,"E4"),sQuery(id+"F2.wireOp",EDGE,"E5"),sQuery(id+"F2.wireOp",EDGE,"E6"),sQuery(id+"F2.wireOp",EDGE,"E7"),sQuery(id+"F2.wireOp",EDGE,"E8"),sQuery(id+"F2.wireOp",EDGE,"E9"),sQuery(id+"F2.wireOp",EDGE,"E10"),sQuery(id+"F2.wireOp",EDGE,"E11"),sQuery(id+"F2.wireOp",EDGE,"E12"),sQuery(id+"F2.wireOp",EDGE,"E13"),sQuery(id+"F2.wireOp",EDGE,"E14"),sQuery(id+"F2.wireOp",EDGE,"E15"),sQuery(id+"F2.wireOp",EDGE,"E16"),sQuery(id+"F2.wireOp",EDGE,"E17"),sQuery(id+"F2.wireOp",EDGE,"E18"),sQuery(id+"F2.wireOp",EDGE,"E19"),sQuery(id+"F2.wireOp",EDGE,"E20"),sQuery(id+"F2.wireOp",EDGE,"E21"),sQuery(id+"F2.wireOp",EDGE,"E22"),sQuery(id+"F2.wireOp",EDGE,"E23"),sQuery(id+"F2.wireOp",EDGE,"E24"),sQuery(id+"F2.wireOp",EDGE,"E25")])],"isStart":false}),makeQuery(id+"F0.opExtrude","SWEPT_FACE",FACE,{"disambiguationData":[OSD([subQ0])]})]});}
            var Q9;
            {var subQ0=sQuery(id+"F2.wireOp",EDGE,"E1");Q9=makeQuery(id+"F0.boolean.opBoolean","INTERSECT",EDGE,{"disambiguationData":[OD(2.0)],"derivedFrom":[makeQuery(id+"F3.opExtrude","CAP_FACE",FACE,{"disambiguationData":[OSD([sQuery(id+"F2.wireOp",EDGE,"E0"),subQ0,sQuery(id+"F2.wireOp",EDGE,"E2"),sQuery(id+"F2.wireOp",EDGE,"E3"),sQuery(id+"F2.wireOp",EDGE,"E4"),sQuery(id+"F2.wireOp",EDGE,"E5"),sQuery(id+"F2.wireOp",EDGE,"E6"),sQuery(id+"F2.wireOp",EDGE,"E7"),sQuery(id+"F2.wireOp",EDGE,"E8"),sQuery(id+"F2.wireOp",EDGE,"E9"),sQuery(id+"F2.wireOp",EDGE,"E10"),sQuery(id+"F2.wireOp",EDGE,"E11"),sQuery(id+"F2.wireOp",EDGE,"E12"),sQuery(id+"F2.wireOp",EDGE,"E13"),sQuery(id+"F2.wireOp",EDGE,"E14"),sQuery(id+"F2.wireOp",EDGE,"E15"),sQuery(id+"F2.wireOp",EDGE,"E16"),sQuery(id+"F2.wireOp",EDGE,"E17"),sQuery(id+"F2.wireOp",EDGE,"E18"),sQuery(id+"F2.wireOp",EDGE,"E19"),sQuery(id+"F2.wireOp",EDGE,"E20"),sQuery(id+"F2.wireOp",EDGE,"E21"),sQuery(id+"F2.wireOp",EDGE,"E22"),sQuery(id+"F2.wireOp",EDGE,"E23"),sQuery(id+"F2.wireOp",EDGE,"E24"),sQuery(id+"F2.wireOp",EDGE,"E25")])],"isStart":false}),makeQuery(id+"F0.opExtrude","SWEPT_FACE",FACE,{"disambiguationData":[OSD([subQ0])]})]});}
            var Q10;
            {var subQ0=sQuery(id+"F2.wireOp",EDGE,"E2");Q10=makeQuery(id+"F0.boolean.opBoolean","INTERSECT",EDGE,{"disambiguationData":[OD(1.0)],"derivedFrom":[makeQuery(id+"F3.opExtrude","CAP_FACE",FACE,{"disambiguationData":[OSD([sQuery(id+"F2.wireOp",EDGE,"E0"),sQuery(id+"F2.wireOp",EDGE,"E1"),subQ0,sQuery(id+"F2.wireOp",EDGE,"E3"),sQuery(id+"F2.wireOp",EDGE,"E4"),sQuery(id+"F2.wireOp",EDGE,"E5"),sQuery(id+"F2.wireOp",EDGE,"E6"),sQuery(id+"F2.wireOp",EDGE,"E7"),sQuery(id+"F2.wireOp",EDGE,"E8"),sQuery(id+"F2.wireOp",EDGE,"E9"),sQuery(id+"F2.wireOp",EDGE,"E10"),sQuery(id+"F2.wireOp",EDGE,"E11"),sQuery(id+"F2.wireOp",EDGE,"E12"),sQuery(id+"F2.wireOp",EDGE,"E13"),sQuery(id+"F2.wireOp",EDGE,"E14"),sQuery(id+"F2.wireOp",EDGE,"E15"),sQuery(id+"F2.wireOp",EDGE,"E16"),sQuery(id+"F2.wireOp",EDGE,"E17"),sQuery(id+"F2.wireOp",EDGE,"E18"),sQuery(id+"F2.wireOp",EDGE,"E19"),sQuery(id+"F2.wireOp",EDGE,"E20"),sQuery(id+"F2.wireOp",EDGE,"E21"),sQuery(id+"F2.wireOp",EDGE,"E22"),sQuery(id+"F2.wireOp",EDGE,"E23"),sQuery(id+"F2.wireOp",EDGE,"E24"),sQuery(id+"F2.wireOp",EDGE,"E25")])],"isStart":false}),makeQuery(id+"F0.opExtrude","SWEPT_FACE",FACE,{"disambiguationData":[OSD([subQ0])]})]});}
            var Q11;
            {var subQ0=sQuery(id+"F2.wireOp",EDGE,"E4");Q11=makeQuery(id+"F0.boolean.opBoolean","INTERSECT",EDGE,{"disambiguationData":[OD(1.0)],"derivedFrom":[makeQuery(id+"F3.opExtrude","CAP_FACE",FACE,{"disambiguationData":[OSD([sQuery(id+"F2.wireOp",EDGE,"E0"),sQuery(id+"F2.wireOp",EDGE,"E1"),sQuery(id+"F2.wireOp",EDGE,"E2"),sQuery(id+"F2.wireOp",EDGE,"E3"),subQ0,sQuery(id+"F2.wireOp",EDGE,"E5"),sQuery(id+"F2.wireOp",EDGE,"E6"),sQuery(id+"F2.wireOp",EDGE,"E7"),sQuery(id+"F2.wireOp",EDGE,"E8"),sQuery(id+"F2.wireOp",EDGE,"E9"),sQuery(id+"F2.wireOp",EDGE,"E10"),sQuery(id+"F2.wireOp",EDGE,"E11"),sQuery(id+"F2.wireOp",EDGE,"E12"),sQuery(id+"F2.wireOp",EDGE,"E13"),sQuery(id+"F2.wireOp",EDGE,"E14"),sQuery(id+"F2.wireOp",EDGE,"E15"),sQuery(id+"F2.wireOp",EDGE,"E16"),sQuery(id+"F2.wireOp",EDGE,"E17"),sQuery(id+"F2.wireOp",EDGE,"E18"),sQuery(id+"F2.wireOp",EDGE,"E19"),sQuery(id+"F2.wireOp",EDGE,"E20"),sQuery(id+"F2.wireOp",EDGE,"E21"),sQuery(id+"F2.wireOp",EDGE,"E22"),sQuery(id+"F2.wireOp",EDGE,"E23"),sQuery(id+"F2.wireOp",EDGE,"E24"),sQuery(id+"F2.wireOp",EDGE,"E25")])],"isStart":false}),makeQuery(id+"F0.opExtrude","SWEPT_FACE",FACE,{"disambiguationData":[OSD([subQ0])]})]});}
            var Q12;
            {var subQ0=sQuery(id+"F2.wireOp",EDGE,"E5");Q12=makeQuery(id+"F0.boolean.opBoolean","INTERSECT",EDGE,{"disambiguationData":[OD(0.0)],"derivedFrom":[makeQuery(id+"F3.opExtrude","CAP_FACE",FACE,{"disambiguationData":[OSD([sQuery(id+"F2.wireOp",EDGE,"E0"),sQuery(id+"F2.wireOp",EDGE,"E1"),sQuery(id+"F2.wireOp",EDGE,"E2"),sQuery(id+"F2.wireOp",EDGE,"E3"),sQuery(id+"F2.wireOp",EDGE,"E4"),subQ0,sQuery(id+"F2.wireOp",EDGE,"E6"),sQuery(id+"F2.wireOp",EDGE,"E7"),sQuery(id+"F2.wireOp",EDGE,"E8"),sQuery(id+"F2.wireOp",EDGE,"E9"),sQuery(id+"F2.wireOp",EDGE,"E10"),sQuery(id+"F2.wireOp",EDGE,"E11"),sQuery(id+"F2.wireOp",EDGE,"E12"),sQuery(id+"F2.wireOp",EDGE,"E13"),sQuery(id+"F2.wireOp",EDGE,"E14"),sQuery(id+"F2.wireOp",EDGE,"E15"),sQuery(id+"F2.wireOp",EDGE,"E16"),sQuery(id+"F2.wireOp",EDGE,"E17"),sQuery(id+"F2.wireOp",EDGE,"E18"),sQuery(id+"F2.wireOp",EDGE,"E19"),sQuery(id+"F2.wireOp",EDGE,"E20"),sQuery(id+"F2.wireOp",EDGE,"E21"),sQuery(id+"F2.wireOp",EDGE,"E22"),sQuery(id+"F2.wireOp",EDGE,"E23"),sQuery(id+"F2.wireOp",EDGE,"E24"),sQuery(id+"F2.wireOp",EDGE,"E25")])],"isStart":false}),makeQuery(id+"F0.opExtrude","SWEPT_FACE",FACE,{"disambiguationData":[OSD([subQ0])]})]});}
            var Q13;
            {var subQ0=sQuery(id+"F2.wireOp",EDGE,"E3");Q13=makeQuery(id+"F0.boolean.opBoolean","INTERSECT",EDGE,{"disambiguationData":[OD(0.0)],"derivedFrom":[makeQuery(id+"F3.opExtrude","CAP_FACE",FACE,{"disambiguationData":[OSD([sQuery(id+"F2.wireOp",EDGE,"E0"),sQuery(id+"F2.wireOp",EDGE,"E1"),sQuery(id+"F2.wireOp",EDGE,"E2"),subQ0,sQuery(id+"F2.wireOp",EDGE,"E4"),sQuery(id+"F2.wireOp",EDGE,"E5"),sQuery(id+"F2.wireOp",EDGE,"E6"),sQuery(id+"F2.wireOp",EDGE,"E7"),sQuery(id+"F2.wireOp",EDGE,"E8"),sQuery(id+"F2.wireOp",EDGE,"E9"),sQuery(id+"F2.wireOp",EDGE,"E10"),sQuery(id+"F2.wireOp",EDGE,"E11"),sQuery(id+"F2.wireOp",EDGE,"E12"),sQuery(id+"F2.wireOp",EDGE,"E13"),sQuery(id+"F2.wireOp",EDGE,"E14"),sQuery(id+"F2.wireOp",EDGE,"E15"),sQuery(id+"F2.wireOp",EDGE,"E16"),sQuery(id+"F2.wireOp",EDGE,"E17"),sQuery(id+"F2.wireOp",EDGE,"E18"),sQuery(id+"F2.wireOp",EDGE,"E19"),sQuery(id+"F2.wireOp",EDGE,"E20"),sQuery(id+"F2.wireOp",EDGE,"E21"),sQuery(id+"F2.wireOp",EDGE,"E22"),sQuery(id+"F2.wireOp",EDGE,"E23"),sQuery(id+"F2.wireOp",EDGE,"E24"),sQuery(id+"F2.wireOp",EDGE,"E25")])],"isStart":false}),makeQuery(id+"F0.opExtrude","SWEPT_FACE",FACE,{"disambiguationData":[OSD([subQ0])]})]});}
            var Q14;
            {var subQ0=sQuery(id+"F2.wireOp",EDGE,"E1");Q14=makeQuery(id+"F0.boolean.opBoolean","INTERSECT",EDGE,{"disambiguationData":[OD(0.0)],"derivedFrom":[makeQuery(id+"F3.opExtrude","CAP_FACE",FACE,{"disambiguationData":[OSD([sQuery(id+"F2.wireOp",EDGE,"E0"),subQ0,sQuery(id+"F2.wireOp",EDGE,"E2"),sQuery(id+"F2.wireOp",EDGE,"E3"),sQuery(id+"F2.wireOp",EDGE,"E4"),sQuery(id+"F2.wireOp",EDGE,"E5"),sQuery(id+"F2.wireOp",EDGE,"E6"),sQuery(id+"F2.wireOp",EDGE,"E7"),sQuery(id+"F2.wireOp",EDGE,"E8"),sQuery(id+"F2.wireOp",EDGE,"E9"),sQuery(id+"F2.wireOp",EDGE,"E10"),sQuery(id+"F2.wireOp",EDGE,"E11"),sQuery(id+"F2.wireOp",EDGE,"E12"),sQuery(id+"F2.wireOp",EDGE,"E13"),sQuery(id+"F2.wireOp",EDGE,"E14"),sQuery(id+"F2.wireOp",EDGE,"E15"),sQuery(id+"F2.wireOp",EDGE,"E16"),sQuery(id+"F2.wireOp",EDGE,"E17"),sQuery(id+"F2.wireOp",EDGE,"E18"),sQuery(id+"F2.wireOp",EDGE,"E19"),sQuery(id+"F2.wireOp",EDGE,"E20"),sQuery(id+"F2.wireOp",EDGE,"E21"),sQuery(id+"F2.wireOp",EDGE,"E22"),sQuery(id+"F2.wireOp",EDGE,"E23"),sQuery(id+"F2.wireOp",EDGE,"E24"),sQuery(id+"F2.wireOp",EDGE,"E25")])],"isStart":false}),makeQuery(id+"F0.opExtrude","SWEPT_FACE",FACE,{"disambiguationData":[OSD([subQ0])]})]});}
            var Q15;
            {var subQ0=sQuery(id+"F2.wireOp",EDGE,"E2");Q15=makeQuery(id+"F0.boolean.opBoolean","INTERSECT",EDGE,{"disambiguationData":[OD(2.0)],"derivedFrom":[makeQuery(id+"F3.opExtrude","CAP_FACE",FACE,{"disambiguationData":[OSD([sQuery(id+"F2.wireOp",EDGE,"E0"),sQuery(id+"F2.wireOp",EDGE,"E1"),subQ0,sQuery(id+"F2.wireOp",EDGE,"E3"),sQuery(id+"F2.wireOp",EDGE,"E4"),sQuery(id+"F2.wireOp",EDGE,"E5"),sQuery(id+"F2.wireOp",EDGE,"E6"),sQuery(id+"F2.wireOp",EDGE,"E7"),sQuery(id+"F2.wireOp",EDGE,"E8"),sQuery(id+"F2.wireOp",EDGE,"E9"),sQuery(id+"F2.wireOp",EDGE,"E10"),sQuery(id+"F2.wireOp",EDGE,"E11"),sQuery(id+"F2.wireOp",EDGE,"E12"),sQuery(id+"F2.wireOp",EDGE,"E13"),sQuery(id+"F2.wireOp",EDGE,"E14"),sQuery(id+"F2.wireOp",EDGE,"E15"),sQuery(id+"F2.wireOp",EDGE,"E16"),sQuery(id+"F2.wireOp",EDGE,"E17"),sQuery(id+"F2.wireOp",EDGE,"E18"),sQuery(id+"F2.wireOp",EDGE,"E19"),sQuery(id+"F2.wireOp",EDGE,"E20"),sQuery(id+"F2.wireOp",EDGE,"E21"),sQuery(id+"F2.wireOp",EDGE,"E22"),sQuery(id+"F2.wireOp",EDGE,"E23"),sQuery(id+"F2.wireOp",EDGE,"E24"),sQuery(id+"F2.wireOp",EDGE,"E25")])],"isStart":false}),makeQuery(id+"F0.opExtrude","SWEPT_FACE",FACE,{"disambiguationData":[OSD([subQ0])]})]});}
            var Q16;
            {var subQ0=sQuery(id+"F2.wireOp",EDGE,"E4");Q16=makeQuery(id+"F0.boolean.opBoolean","INTERSECT",EDGE,{"disambiguationData":[OD(2.0)],"derivedFrom":[makeQuery(id+"F3.opExtrude","CAP_FACE",FACE,{"disambiguationData":[OSD([sQuery(id+"F2.wireOp",EDGE,"E0"),sQuery(id+"F2.wireOp",EDGE,"E1"),sQuery(id+"F2.wireOp",EDGE,"E2"),sQuery(id+"F2.wireOp",EDGE,"E3"),subQ0,sQuery(id+"F2.wireOp",EDGE,"E5"),sQuery(id+"F2.wireOp",EDGE,"E6"),sQuery(id+"F2.wireOp",EDGE,"E7"),sQuery(id+"F2.wireOp",EDGE,"E8"),sQuery(id+"F2.wireOp",EDGE,"E9"),sQuery(id+"F2.wireOp",EDGE,"E10"),sQuery(id+"F2.wireOp",EDGE,"E11"),sQuery(id+"F2.wireOp",EDGE,"E12"),sQuery(id+"F2.wireOp",EDGE,"E13"),sQuery(id+"F2.wireOp",EDGE,"E14"),sQuery(id+"F2.wireOp",EDGE,"E15"),sQuery(id+"F2.wireOp",EDGE,"E16"),sQuery(id+"F2.wireOp",EDGE,"E17"),sQuery(id+"F2.wireOp",EDGE,"E18"),sQuery(id+"F2.wireOp",EDGE,"E19"),sQuery(id+"F2.wireOp",EDGE,"E20"),sQuery(id+"F2.wireOp",EDGE,"E21"),sQuery(id+"F2.wireOp",EDGE,"E22"),sQuery(id+"F2.wireOp",EDGE,"E23"),sQuery(id+"F2.wireOp",EDGE,"E24"),sQuery(id+"F2.wireOp",EDGE,"E25")])],"isStart":false}),makeQuery(id+"F0.opExtrude","SWEPT_FACE",FACE,{"disambiguationData":[OSD([subQ0])]})]});}
            var Q17;
            {var subQ0=sQuery(id+"F2.wireOp",EDGE,"E5");Q17=makeQuery(id+"F0.boolean.opBoolean","INTERSECT",EDGE,{"disambiguationData":[OD(3.0)],"derivedFrom":[makeQuery(id+"F3.opExtrude","CAP_FACE",FACE,{"disambiguationData":[OSD([sQuery(id+"F2.wireOp",EDGE,"E0"),sQuery(id+"F2.wireOp",EDGE,"E1"),sQuery(id+"F2.wireOp",EDGE,"E2"),sQuery(id+"F2.wireOp",EDGE,"E3"),sQuery(id+"F2.wireOp",EDGE,"E4"),subQ0,sQuery(id+"F2.wireOp",EDGE,"E6"),sQuery(id+"F2.wireOp",EDGE,"E7"),sQuery(id+"F2.wireOp",EDGE,"E8"),sQuery(id+"F2.wireOp",EDGE,"E9"),sQuery(id+"F2.wireOp",EDGE,"E10"),sQuery(id+"F2.wireOp",EDGE,"E11"),sQuery(id+"F2.wireOp",EDGE,"E12"),sQuery(id+"F2.wireOp",EDGE,"E13"),sQuery(id+"F2.wireOp",EDGE,"E14"),sQuery(id+"F2.wireOp",EDGE,"E15"),sQuery(id+"F2.wireOp",EDGE,"E16"),sQuery(id+"F2.wireOp",EDGE,"E17"),sQuery(id+"F2.wireOp",EDGE,"E18"),sQuery(id+"F2.wireOp",EDGE,"E19"),sQuery(id+"F2.wireOp",EDGE,"E20"),sQuery(id+"F2.wireOp",EDGE,"E21"),sQuery(id+"F2.wireOp",EDGE,"E22"),sQuery(id+"F2.wireOp",EDGE,"E23"),sQuery(id+"F2.wireOp",EDGE,"E24"),sQuery(id+"F2.wireOp",EDGE,"E25")])],"isStart":false}),makeQuery(id+"F0.opExtrude","SWEPT_FACE",FACE,{"disambiguationData":[OSD([subQ0])]})]});}
            var Q18;
            {var subQ0=sQuery(id+"F2.wireOp",EDGE,"E3");Q18=makeQuery(id+"F0.boolean.opBoolean","INTERSECT",EDGE,{"disambiguationData":[OD(3.0)],"derivedFrom":[makeQuery(id+"F3.opExtrude","CAP_FACE",FACE,{"disambiguationData":[OSD([sQuery(id+"F2.wireOp",EDGE,"E0"),sQuery(id+"F2.wireOp",EDGE,"E1"),sQuery(id+"F2.wireOp",EDGE,"E2"),subQ0,sQuery(id+"F2.wireOp",EDGE,"E4"),sQuery(id+"F2.wireOp",EDGE,"E5"),sQuery(id+"F2.wireOp",EDGE,"E6"),sQuery(id+"F2.wireOp",EDGE,"E7"),sQuery(id+"F2.wireOp",EDGE,"E8"),sQuery(id+"F2.wireOp",EDGE,"E9"),sQuery(id+"F2.wireOp",EDGE,"E10"),sQuery(id+"F2.wireOp",EDGE,"E11"),sQuery(id+"F2.wireOp",EDGE,"E12"),sQuery(id+"F2.wireOp",EDGE,"E13"),sQuery(id+"F2.wireOp",EDGE,"E14"),sQuery(id+"F2.wireOp",EDGE,"E15"),sQuery(id+"F2.wireOp",EDGE,"E16"),sQuery(id+"F2.wireOp",EDGE,"E17"),sQuery(id+"F2.wireOp",EDGE,"E18"),sQuery(id+"F2.wireOp",EDGE,"E19"),sQuery(id+"F2.wireOp",EDGE,"E20"),sQuery(id+"F2.wireOp",EDGE,"E21"),sQuery(id+"F2.wireOp",EDGE,"E22"),sQuery(id+"F2.wireOp",EDGE,"E23"),sQuery(id+"F2.wireOp",EDGE,"E24"),sQuery(id+"F2.wireOp",EDGE,"E25")])],"isStart":false}),makeQuery(id+"F0.opExtrude","SWEPT_FACE",FACE,{"disambiguationData":[OSD([subQ0])]})]});}
            var Q19;
            {var subQ0=sQuery(id+"F2.wireOp",EDGE,"E1");Q19=makeQuery(id+"F0.boolean.opBoolean","INTERSECT",EDGE,{"disambiguationData":[OD(3.0)],"derivedFrom":[makeQuery(id+"F3.opExtrude","CAP_FACE",FACE,{"disambiguationData":[OSD([sQuery(id+"F2.wireOp",EDGE,"E0"),subQ0,sQuery(id+"F2.wireOp",EDGE,"E2"),sQuery(id+"F2.wireOp",EDGE,"E3"),sQuery(id+"F2.wireOp",EDGE,"E4"),sQuery(id+"F2.wireOp",EDGE,"E5"),sQuery(id+"F2.wireOp",EDGE,"E6"),sQuery(id+"F2.wireOp",EDGE,"E7"),sQuery(id+"F2.wireOp",EDGE,"E8"),sQuery(id+"F2.wireOp",EDGE,"E9"),sQuery(id+"F2.wireOp",EDGE,"E10"),sQuery(id+"F2.wireOp",EDGE,"E11"),sQuery(id+"F2.wireOp",EDGE,"E12"),sQuery(id+"F2.wireOp",EDGE,"E13"),sQuery(id+"F2.wireOp",EDGE,"E14"),sQuery(id+"F2.wireOp",EDGE,"E15"),sQuery(id+"F2.wireOp",EDGE,"E16"),sQuery(id+"F2.wireOp",EDGE,"E17"),sQuery(id+"F2.wireOp",EDGE,"E18"),sQuery(id+"F2.wireOp",EDGE,"E19"),sQuery(id+"F2.wireOp",EDGE,"E20"),sQuery(id+"F2.wireOp",EDGE,"E21"),sQuery(id+"F2.wireOp",EDGE,"E22"),sQuery(id+"F2.wireOp",EDGE,"E23"),sQuery(id+"F2.wireOp",EDGE,"E24"),sQuery(id+"F2.wireOp",EDGE,"E25")])],"isStart":false}),makeQuery(id+"F0.opExtrude","SWEPT_FACE",FACE,{"disambiguationData":[OSD([subQ0])]})]});}
            fillet(context, id + "F4", {"entities" : qUnion([Q0, Q1, Q2, Q3, Q4, Q5, Q6, Q7, Q8, Q9, Q10, Q11, Q12, Q13, Q14, Q15, Q16, Q17, Q18, Q19]), "radius" : 3 * mm, "tangentPropagation" : true, "allowEdgeOverflow" : false});
        }
    });
